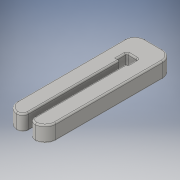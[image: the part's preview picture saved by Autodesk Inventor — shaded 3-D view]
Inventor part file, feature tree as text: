
AUTODESK INVENTOR PART (.ipt)
format: ipt  version: 2016 (Build 200138000, 138)  size: 187,392 bytes
history: native  units: in
note: dims shown in document units (in); Inventor stores cm internally (conversion verified against a paired STEP export)
features: fillet x4, extrude x1, sketch x1
ambient origin geometry x8: Origin, YZ Plane, XZ Plane, XY Plane, X Axis, Y Axis, Z Axis, Center Point
bodies: Solid1 (feature_tree)
feature tree (6):
  extrude  "Extrusion1"  Depth=0.25in
  fillet  "Fillet1"  Radius=0.1875in
  fillet  "Fillet2"  Radius=0.1875in
  fillet  "Fillet3"  Radius=0.125in
  fillet  "Fillet4"  Radius=0.068in
  sketch  "Sketch1"  dims[d12=1.5in d13=0.25in d14=0.1875in d15=0.1875in d16=0.0in d17=0.125in d18=0.068in d19=0.017in d20=0.125in d21=0.125in d22=0.075in d23=0.1562in d24=1.25in d25=0.0687in d26=0.1875in d27=1.125in d28=0.017in]
